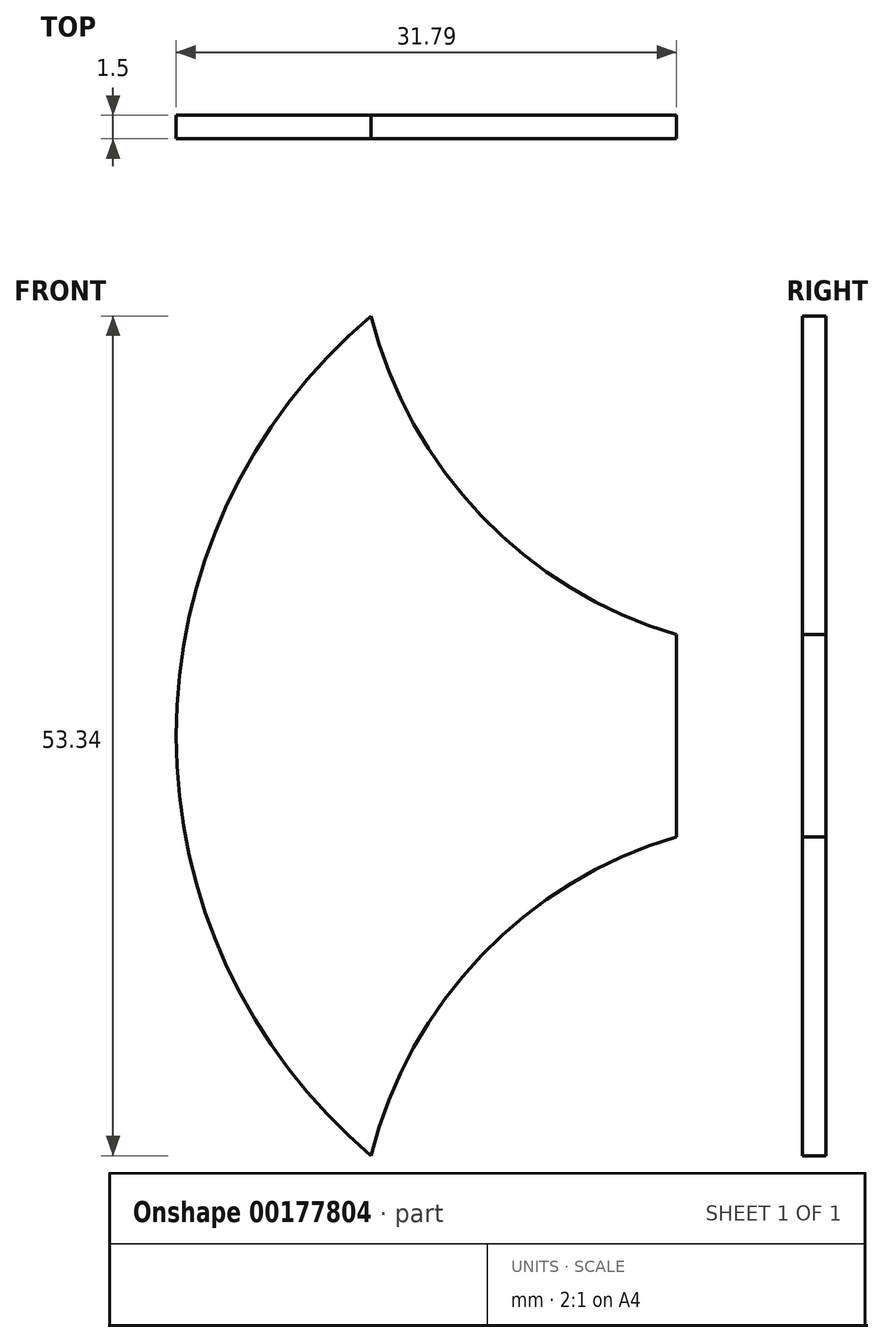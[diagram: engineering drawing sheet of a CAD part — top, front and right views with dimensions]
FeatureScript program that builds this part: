
annotation { "Feature Type Name" : "Feature", "Feature Type Description" : "" }
export const myFeature = defineFeature(function(context is Context, id is Id, definition is map)
    precondition{}
    {
        {
            var Q0;
            Q0=qCreatedBy(makeId("Front.planeOp"),FACE);
            var sketch = newSketch(context, id + "F0", { "sketchPlane" : qUnion([Q0])});
            skLineSegment(sketch, "E0", {"start": v(0, 0) * mm, "end": v(0, 6.42) * mm});
            skArc(sketch, "E1", {"start": v(-19.4, 26.67) * mm, "mid": v(-12.4, 13.96) * mm, "end": v(0, 6.42) * mm});
            skArc(sketch, "E2.MirrorCS", {"start": v(-19.4, -26.67) * mm, "mid": v(-12.4, -13.96) * mm, "end": v(0, -6.42) * mm});
            skLineSegment(sketch, "E3.MirrorCS", {"start": v(0, 0) * mm, "end": v(0, -6.42) * mm});
            skArc(sketch, "E4", {"start": v(-19.4, 26.67) * mm, "mid": v(-31.79, 0) * mm, "end": v(-19.4, -26.67) * mm});
            skSolve(sketch);
        }
        {
            var Q0;
            Q0=makeQuery(id+"F0.imprint","IMPRINT",FACE,{"disambiguationData":[TD([[makeQuery(id+"F0.imprint","IMPRINT",EDGE,{"derivedFrom":sQuery(id+"F0.wireOp",EDGE,"E0")}),1.0]])]});
            extrude(context, id + "F1", {"entities" : qUnion([Q0]), "depth" : 1.5 * mm});
        }
    });
